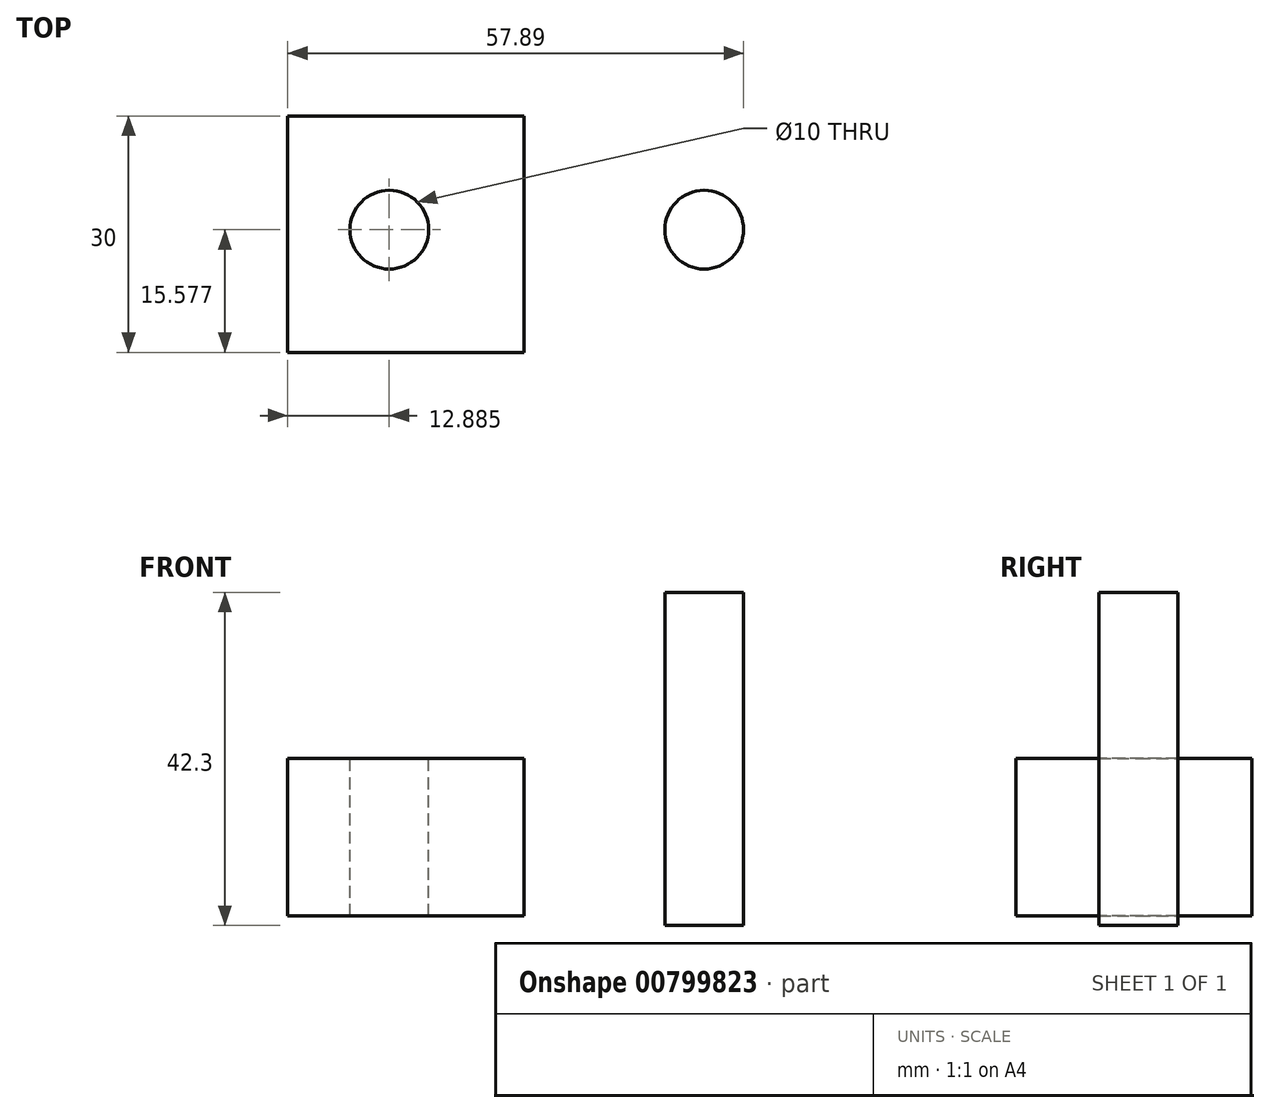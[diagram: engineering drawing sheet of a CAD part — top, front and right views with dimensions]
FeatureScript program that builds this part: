
annotation { "Feature Type Name" : "Feature", "Feature Type Description" : "" }
export const myFeature = defineFeature(function(context is Context, id is Id, definition is map)
    precondition{}
    {
        {
            var Q0;
            Q0=qCreatedBy(makeId("Top.planeOp"),FACE);
            var sketch = newSketch(context, id + "F0", { "sketchPlane" : qUnion([Q0])});
            skLineSegment(sketch, "E0.bottom", {"start": v(-44.52, 30) * mm, "end": v(-14.52, 30) * mm});
            skLineSegment(sketch, "E0.top", {"start": v(-44.52, 0) * mm, "end": v(-14.52, 0) * mm});
            skLineSegment(sketch, "E0.left", {"start": v(-44.52, 30) * mm, "end": v(-44.52, 0) * mm});
            skLineSegment(sketch, "E0.right", {"start": v(-14.52, 30) * mm, "end": v(-14.52, 0) * mm});
            skSolve(sketch);
        }
        {
            var Q0;
            Q0=makeQuery(id+"F0.imprint","IMPRINT",FACE,{"disambiguationData":[TD([[makeQuery(id+"F0.imprint","IMPRINT",EDGE,{"derivedFrom":sQuery(id+"F0.wireOp",EDGE,"E0.bottom")}),-1.0]])]});
            extrude(context, id + "F1", {"entities" : qUnion([Q0]), "depth" : 20 * mm, "offsetDistance" : 25 * mm, "symmetric" : true});
        }
        {
            var Q0;
            Q0=makeQuery(id+"F1.opExtrude","CAP_FACE",FACE,{"disambiguationData":[OSD([sQuery(id+"F0.wireOp",EDGE,"E0.bottom"),sQuery(id+"F0.wireOp",EDGE,"E0.top"),sQuery(id+"F0.wireOp",EDGE,"E0.left"),sQuery(id+"F0.wireOp",EDGE,"E0.right")])],"isStart":false});
            cPlane(context, id + "F2", {"entities" : qUnion([Q0]), "cplaneType" : CPlaneType.OFFSET, "offset" : 10 * mm, "width" : 150 * mm, "height" : 150 * mm});
        }
        {
            var Q0;
            Q0=qCreatedBy(id+"F2.planeOp",FACE);
            var sketch = newSketch(context, id + "F3", { "sketchPlane" : qUnion([Q0])});
            skCircle(sketch, "E1", {"center": v(-31.63, 15.58) * mm, "radius": 5 * mm});
            skSolve(sketch);
        }
        {
            var Q0;
            Q0=makeQuery(id+"F3.imprint","IMPRINT",FACE,{"disambiguationData":[TD([[makeQuery(id+"F3.imprint","IMPRINT",EDGE,{"derivedFrom":sQuery(id+"F3.wireOp",EDGE,"E1")}),1.0]])]});
            extrude(context, id + "F4", {"entities" : qUnion([Q0]), "oppositeDirection" : true, "depth" : 42.3 * mm, "offsetDistance" : 25 * mm});
        }
        {
            var Q0;
            Q0=makeQuery(id+"F4.opExtrude","SWEPT_BODY",BODY,{"disambiguationData":[OSD([sQuery(id+"F3.wireOp",EDGE,"E1")])]});
            var Q1;
            Q1=makeQuery(id+"F1.opExtrude","SWEPT_BODY",BODY,{"disambiguationData":[OSD([sQuery(id+"F0.wireOp",EDGE,"E0.bottom"),sQuery(id+"F0.wireOp",EDGE,"E0.top"),sQuery(id+"F0.wireOp",EDGE,"E0.left"),sQuery(id+"F0.wireOp",EDGE,"E0.right")])]});
            booleanBodies(context, id + "F5", {"operationType" : BooleanOperationType.SUBTRACTION, "tools" : qUnion([Q0]), "targets" : qUnion([Q1]), "keepTools" : true});
        }
        {
            var Q0;
            Q0=makeQuery(id+"F4.opExtrude","SWEPT_BODY",BODY,{"disambiguationData":[OSD([sQuery(id+"F3.wireOp",EDGE,"E1")])]});
            transform(context, id + "F6", {"entities" : qUnion([Q0]), "transformType" : TransformType.TRANSLATION_3D, "dx" : 40 * mm, "dy" : 0 * mm, "dz" : 11.1 * mm, "makeCopy" : false});
        }
    });
